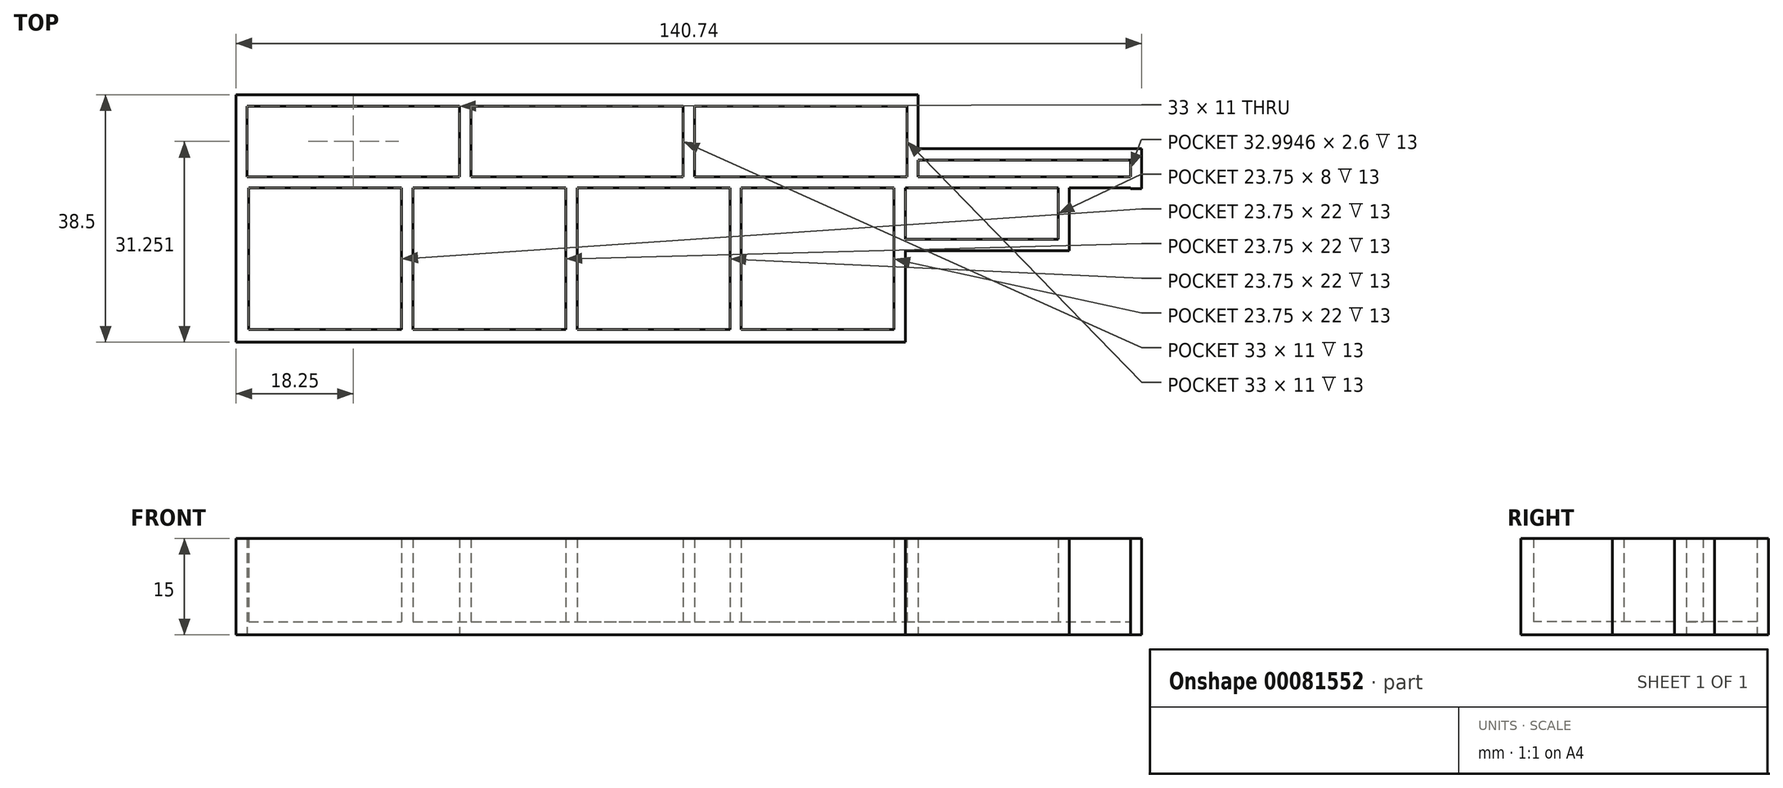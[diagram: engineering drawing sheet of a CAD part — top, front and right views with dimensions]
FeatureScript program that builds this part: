
annotation { "Feature Type Name" : "Feature", "Feature Type Description" : "" }
export const myFeature = defineFeature(function(context is Context, id is Id, definition is map)
    precondition{}
    {
        {
            var Q0;
            Q0=qCreatedBy(makeId("Top.planeOp"),FACE);
            var sketch = newSketch(context, id + "F0", { "sketchPlane" : qUnion([Q0])});
            skLineSegment(sketch, "E0.bottom", {"start": v(-33, 13.96) * mm, "end": v(0, 13.96) * mm});
            skLineSegment(sketch, "E0.top", {"start": v(-34.75, -11.79) * mm, "end": v(69.25, -11.79) * mm});
            skLineSegment(sketch, "E0.left", {"start": v(-34.75, 13.96) * mm, "end": v(-34.75, -11.79) * mm});
            skLineSegment(sketch, "E0.right", {"start": v(69.25, 12.21) * mm, "end": v(69.25, 4.21) * mm});
            skLineSegment(sketch, "E1.bottom", {"start": v(-32.75, 12.21) * mm, "end": v(-9, 12.21) * mm});
            skLineSegment(sketch, "E1.top", {"start": v(-32.75, -9.79) * mm, "end": v(-9, -9.79) * mm});
            skLineSegment(sketch, "E1.left", {"start": v(-34.75, 12.21) * mm, "end": v(-34.75, -9.79) * mm});
            skLineSegment(sketch, "E2.left", {"start": v(-32.75, 12.21) * mm, "end": v(-32.75, -9.79) * mm});
            skLineSegment(sketch, "E3.bottom", {"start": v(-19.34, 12.21) * mm, "end": v(-9, 12.21) * mm});
            skLineSegment(sketch, "E3.top", {"start": v(-19.34, -9.79) * mm, "end": v(-9, -9.79) * mm});
            skLineSegment(sketch, "E3.left", {"start": v(-9, 12.21) * mm, "end": v(-9, -9.79) * mm});
            skLineSegment(sketch, "E4.bottom", {"start": v(-7.25, 12.21) * mm, "end": v(16.5, 12.21) * mm});
            skLineSegment(sketch, "E4.top", {"start": v(-7.25, -9.79) * mm, "end": v(16.5, -9.79) * mm});
            skLineSegment(sketch, "E4.left", {"start": v(-7.25, 12.21) * mm, "end": v(-7.25, -9.79) * mm});
            skLineSegment(sketch, "E4.right", {"start": v(16.5, 12.21) * mm, "end": v(16.5, -9.79) * mm});
            skLineSegment(sketch, "E5.bottom", {"start": v(18.25, 12.21) * mm, "end": v(42, 12.21) * mm});
            skLineSegment(sketch, "E5.top", {"start": v(18.25, -9.79) * mm, "end": v(42, -9.79) * mm});
            skLineSegment(sketch, "E5.left", {"start": v(18.25, 12.21) * mm, "end": v(18.25, -9.79) * mm});
            skLineSegment(sketch, "E5.right", {"start": v(42, 12.21) * mm, "end": v(42, -9.79) * mm});
            skLineSegment(sketch, "E6.bottom", {"start": v(43.75, 12.21) * mm, "end": v(67.5, 12.21) * mm});
            skLineSegment(sketch, "E6.top", {"start": v(43.75, -9.79) * mm, "end": v(67.5, -9.79) * mm});
            skLineSegment(sketch, "E6.left", {"start": v(43.75, 12.21) * mm, "end": v(43.75, -9.79) * mm});
            skLineSegment(sketch, "E6.right", {"start": v(67.5, 12.21) * mm, "end": v(67.5, -9.79) * mm});
            skPoint(sketch, "E7.orphan", {"position": v(69.25, 12.21) * mm});
            skLineSegment(sketch, "E8.top", {"start": v(-33, 24.96) * mm, "end": v(0, 24.96) * mm});
            skLineSegment(sketch, "E8.left", {"start": v(-34.75, 13.96) * mm, "end": v(-34.75, 24.96) * mm});
            skLineSegment(sketch, "E9.left", {"start": v(-33, 24.96) * mm, "end": v(-33, 13.96) * mm});
            skLineSegment(sketch, "E9.right", {"start": v(0, 24.96) * mm, "end": v(0, 13.96) * mm});
            skLineSegment(sketch, "E10.bottom", {"start": v(1.75, 24.96) * mm, "end": v(34.75, 24.96) * mm});
            skLineSegment(sketch, "E10.top", {"start": v(1.75, 13.96) * mm, "end": v(34.75, 13.96) * mm});
            skLineSegment(sketch, "E10.left", {"start": v(1.75, 24.96) * mm, "end": v(1.75, 13.96) * mm});
            skLineSegment(sketch, "E11.bottom", {"start": v(24.2, 24.96) * mm, "end": v(34.75, 24.96) * mm});
            skLineSegment(sketch, "E11.top", {"start": v(24.2, 13.96) * mm, "end": v(34.75, 13.96) * mm});
            skLineSegment(sketch, "E11.left", {"start": v(34.75, 24.96) * mm, "end": v(34.75, 13.96) * mm});
            skLineSegment(sketch, "E12.bottom", {"start": v(36.5, 24.96) * mm, "end": v(69.5, 24.96) * mm});
            skLineSegment(sketch, "E12.top", {"start": v(36.5, 13.96) * mm, "end": v(69.5, 13.96) * mm});
            skLineSegment(sketch, "E12.left", {"start": v(36.5, 24.96) * mm, "end": v(36.5, 13.96) * mm});
            skLineSegment(sketch, "E12.right", {"start": v(69.5, 24.96) * mm, "end": v(69.5, 13.96) * mm});
            skLineSegment(sketch, "E13.top", {"start": v(71.25, 13.96) * mm, "end": v(102.25, 13.96) * mm});
            skLineSegment(sketch, "E14.bottom", {"start": v(69.25, 12.21) * mm, "end": v(93, 12.21) * mm});
            skLineSegment(sketch, "E14.top", {"start": v(63.25, 13.96) * mm, "end": v(69.5, 13.96) * mm});
            skLineSegment(sketch, "E15.trimOffspring", {"start": v(36.5, 13.96) * mm, "end": v(69.25, 13.96) * mm});
            skLineSegment(sketch, "E16.bottom", {"start": v(71.25, 13.96) * mm, "end": v(104.24, 13.96) * mm});
            skLineSegment(sketch, "E16.top", {"start": v(71.25, 16.56) * mm, "end": v(104.24, 16.56) * mm});
            skLineSegment(sketch, "E16.left", {"start": v(71.25, 13.96) * mm, "end": v(71.25, 16.56) * mm});
            skLineSegment(sketch, "E16.right", {"start": v(104.24, 13.96) * mm, "end": v(104.24, 16.56) * mm});
            skLineSegment(sketch, "E17.bottom", {"start": v(71.25, 18.31) * mm, "end": v(104.25, 18.31) * mm});
            skLineSegment(sketch, "E17.left", {"start": v(69.5, 18.31) * mm, "end": v(69.5, 16.56) * mm});
            skLineSegment(sketch, "E18.left", {"start": v(69.5, 24.96) * mm, "end": v(69.5, 16.56) * mm});
            skLineSegment(sketch, "E18.right", {"start": v(71.25, 24.96) * mm, "end": v(71.25, 18.31) * mm});
            skLineSegment(sketch, "E19.bottom", {"start": v(69.5, 24.96) * mm, "end": v(36.5, 24.96) * mm});
            skLineSegment(sketch, "E19.top", {"start": v(71.25, 26.71) * mm, "end": v(-26.96, 26.71) * mm});
            skLineSegment(sketch, "E19.left", {"start": v(71.25, 24.96) * mm, "end": v(71.25, 26.71) * mm});
            skLineSegment(sketch, "E20.bottom", {"start": v(-26.96, 26.71) * mm, "end": v(-34.75, 26.71) * mm});
            skLineSegment(sketch, "E20.top", {"start": v(-26.96, 24.96) * mm, "end": v(-33, 24.96) * mm});
            skLineSegment(sketch, "E20.right", {"start": v(-34.75, 26.71) * mm, "end": v(-34.75, 24.96) * mm});
            skLineSegment(sketch, "E21.trimOffspring", {"start": v(34.75, 24.96) * mm, "end": v(1.75, 24.96) * mm});
            skLineSegment(sketch, "E22.trimOffspring", {"start": v(1.75, 13.96) * mm, "end": v(32.82, 13.96) * mm});
            skLineSegment(sketch, "E23.trimOffspring", {"start": v(0, 24.96) * mm, "end": v(-26.96, 24.96) * mm});
            skLineSegment(sketch, "E24.trimOffspring", {"start": v(1.75, 24.96) * mm, "end": v(32.82, 24.96) * mm});
            skLineSegment(sketch, "E25.bottom", {"start": v(69.25, 4.21) * mm, "end": v(93, 4.21) * mm});
            skLineSegment(sketch, "E25.left", {"start": v(69.25, 4.21) * mm, "end": v(69.25, 12.21) * mm});
            skLineSegment(sketch, "E25.right", {"start": v(93, 4.21) * mm, "end": v(93, 12.21) * mm});
            skLineSegment(sketch, "E26.top", {"start": v(69.25, 2.46) * mm, "end": v(94.75, 2.46) * mm});
            skLineSegment(sketch, "E27.trimOffspring", {"start": v(87.25, 12.21) * mm, "end": v(93, 12.21) * mm});
            skLineSegment(sketch, "E28.trimOffspring", {"start": v(69.25, 2.46) * mm, "end": v(69.25, -11.79) * mm});
            skLineSegment(sketch, "E29.right", {"start": v(61.2, 63.86) * mm, "end": v(61.2, 63.86) * mm});
            skPoint(sketch, "E13.right.start.orphan", {"position": v(104.25, 16.56) * mm});
            skLineSegment(sketch, "E30.bottom", {"start": v(104.25, 18.31) * mm, "end": v(106, 18.31) * mm});
            skLineSegment(sketch, "E30.top", {"start": v(104.25, 12.13) * mm, "end": v(106, 12.13) * mm});
            skLineSegment(sketch, "E30.left", {"start": v(104.25, 12.21) * mm, "end": v(104.25, 12.13) * mm});
            skLineSegment(sketch, "E30.right", {"start": v(106, 18.31) * mm, "end": v(106, 12.13) * mm});
            skLineSegment(sketch, "E31", {"start": v(94.75, 2.46) * mm, "end": v(94.75, 12.21) * mm});
            skLineSegment(sketch, "E32.trimOffspring", {"start": v(94.75, 12.21) * mm, "end": v(104.25, 12.21) * mm});
            skSolve(sketch);
        }
        {
            var Q0;
            {var subQ8=sQuery(id+"F0.wireOp",EDGE,"E0.top");Q0=makeQuery(id+"F0.imprint","IMPRINT",FACE,{"disambiguationData":[TD([[makeQuery(id+"F0.imprint","IMPRINT",EDGE,{"derivedFrom":subQ8}),1.0]])]});}
            extrude(context, id + "F1", {"entities" : qUnion([Q0]), "depth" : 15 * mm});
        }
        {
            var Q0;
            Q0 = qSketchRegion(id + "F0", true);
            var Q1;
            Q1=makeQuery(id+"F0.imprint","IMPRINT",FACE,{"disambiguationData":[TD([[makeQuery(id+"F0.imprint","IMPRINT",EDGE,{"derivedFrom":sQuery(id+"F0.wireOp",EDGE,"E16.bottom")}),1.0]])]});
            extrude(context, id + "F2", {"entities" : qUnion([Q0, Q1]), "operationType" : NewBodyOperationType.ADD, "depth" : 2 * mm});
        }
        {
            var Q0;
            Q0=makeQuery(id+"F0.imprint","IMPRINT",FACE,{"disambiguationData":[TD([[makeQuery(id+"F0.imprint","IMPRINT",EDGE,{"derivedFrom":sQuery(id+"F0.wireOp",EDGE,"E12.left")}),1.0]])]});
            var Q1;
            Q1=makeQuery(id+"F0.imprint","IMPRINT",FACE,{"disambiguationData":[TD([[makeQuery(id+"F0.imprint","IMPRINT",EDGE,{"derivedFrom":sQuery(id+"F0.wireOp",EDGE,"E6.left")}),1.0]])]});
            var Q2;
            Q2=makeQuery(id+"F0.imprint","IMPRINT",FACE,{"disambiguationData":[TD([[makeQuery(id+"F0.imprint","IMPRINT",EDGE,{"derivedFrom":sQuery(id+"F0.wireOp",EDGE,"E25.bottom")}),1.0]])]});
            var Q3;
            Q3=makeQuery(id+"F0.imprint","IMPRINT",FACE,{"disambiguationData":[TD([[makeQuery(id+"F0.imprint","IMPRINT",EDGE,{"derivedFrom":sQuery(id+"F0.wireOp",EDGE,"E5.left")}),1.0]])]});
            var Q4;
            {var subQ2=sQuery(id+"F0.wireOp",EDGE,"E10.left");Q4=makeQuery(id+"F0.imprint","IMPRINT",FACE,{"disambiguationData":[TD([[makeQuery(id+"F0.imprint","IMPRINT",EDGE,{"derivedFrom":subQ2}),1.0]])]});}
            var Q5;
            Q5=makeQuery(id+"F0.imprint","IMPRINT",FACE,{"disambiguationData":[TD([[makeQuery(id+"F0.imprint","IMPRINT",EDGE,{"derivedFrom":sQuery(id+"F0.wireOp",EDGE,"E4.left")}),1.0]])]});
            var Q6;
            Q6=makeQuery(id+"F0.imprint","IMPRINT",FACE,{"disambiguationData":[TD([[makeQuery(id+"F0.imprint","IMPRINT",EDGE,{"derivedFrom":sQuery(id+"F0.wireOp",EDGE,"E0.bottom")}),1.0]])]});
            var Q7;
            Q7=makeQuery(id+"F0.imprint","IMPRINT",FACE,{"disambiguationData":[TD([[makeQuery(id+"F0.imprint","IMPRINT",EDGE,{"derivedFrom":sQuery(id+"F0.wireOp",EDGE,"E1.bottom")}),-1.0]])]});
            var Q8;
            Q8=makeQuery(id+"F0.imprint","IMPRINT",FACE,{"disambiguationData":[TD([[makeQuery(id+"F0.imprint","IMPRINT",EDGE,{"derivedFrom":sQuery(id+"F0.wireOp",EDGE,"E16.bottom")}),1.0]])]});
            extrude(context, id + "F3", {"entities" : qUnion([Q0, Q1, Q2, Q3, Q4, Q5, Q6, Q7, Q8]), "operationType" : NewBodyOperationType.ADD, "depth" : 2 * mm});
        }
    });
